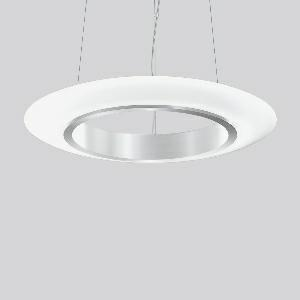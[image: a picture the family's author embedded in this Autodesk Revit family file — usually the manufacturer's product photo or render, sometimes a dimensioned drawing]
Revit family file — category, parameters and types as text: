
# Revit family: ring_of_fire_p_311570_004_2_730_61a7
name_source: partatom
category: Lighting Fixtures
units: mm (PartAtom-declared; Revit-internal decimal feet)

## family parameters
Cut with Voids When Loaded = No
Host = Face
Light Source = No
Part Type = Normal
Room Calculation Point = No
Round Connector Dimension = Use Diameter
Shared = No

## types (1)
- TuneableWhite 846 (1 x LED Modul 846, 3500 lm, 4600)
    Apparent Load = 38 VA
    CIE Flux Codes = 43 73 90 55 100
    Color Rendering = 80
    Color Temperature = 4600
    Default Elevation = 1800 mm
    Description = Series: RING OF FIRE
A uniquely shaped pendant luminaire with elliptical glass. Supporting ring made of anodised aluminium. Canopy aluminium anodised. Opal glass: mouth-blown, satin finish. Tunable white dynamically adjustable from 2700 K to 6500 K. Suitable for pendant. 3-point steel cable suspension, steplessly adjustable. Special lengths available on request. Power supply through separate cable. Converter integrated in the canopy. With Casambi smart+free Bluetooth control for wireless network and operation using Android / iOS devices, free app available for download. 
Colour: anodised aluminium
Diameter: 690 mm
Height: 81 mm
Suspension length: 500-1200 mm
Lamp: LED
Socket: without socket
Colour temperature: 2700K - 6500K
Colour rendering index (CRI): 80
System power: 38 W
Rated luminous flux: 3500 lm
Luminous efficiency: 92 lm/W
System power 2: 38 W
Rated luminous flux 2: 3300 lm
Luminous efficiency 2: 87 lm/W
System power 3: 38 W
Rated luminous flux 3: 3250 lm
Luminous efficiency 3: 86 lm/W
Control gear: Dimmable Bluetooth converter
Protection class: I
Type of protection: IP 20
    Height = 81 mm
    Lamp = 1 x LED Modul 846
    Lamp Light Flux = 3500 lm
    Lamp count = 1
    Length = 690 mm
    Lifetime = 50000 h
    Luminous efficacy = 92 lm/W
    Manufacturer = RZB
    ModVariant = No
    Model = 311570.004.2.730
    Mounting Place = Ceiling
    Mounting Type = Pendant
    Number of Poles = 1
    OnlyDefault = Yes
    Power Factor = 1
    Product Name = RING OF FIRE P
    Product group = Pendant luminaires
    ProductGroupID = 902
    Protection Class = Protection class I
    Protection Degree = IP 20
    RLX_Detail_Level = 1
    RLX_Emergency_Light_Flux = 0 lm
    RLX_Emergency_Type = 0
    RLX_Emergency_Type_DB = No
    RlxData = <blob elided: 31929 chars, md5=ef89783e>
    Socket = socket
    Standby Power = 0 W
    System Light Flux = 3500 lm
    System Power = 38 W
    Type Comments = TuneableWhite 846
    Type Image = 311570.004.jpg
    URL = http://relux.com
    VarID = tuneablewhite_846
    Voltage = 230 V
    Voltage Range = 220-240 V
    Weight = 0.00 kg
    Width = 0 mm  [stored 0 ft]

note: [stored X ft] marks values corroborated as IEEE doubles in the binary element streams (Revit-internal decimal feet)

## geometry (parser evidence)
native form markers: Blend x4, Sweep x11
no freeform markers — native parametric forms only
